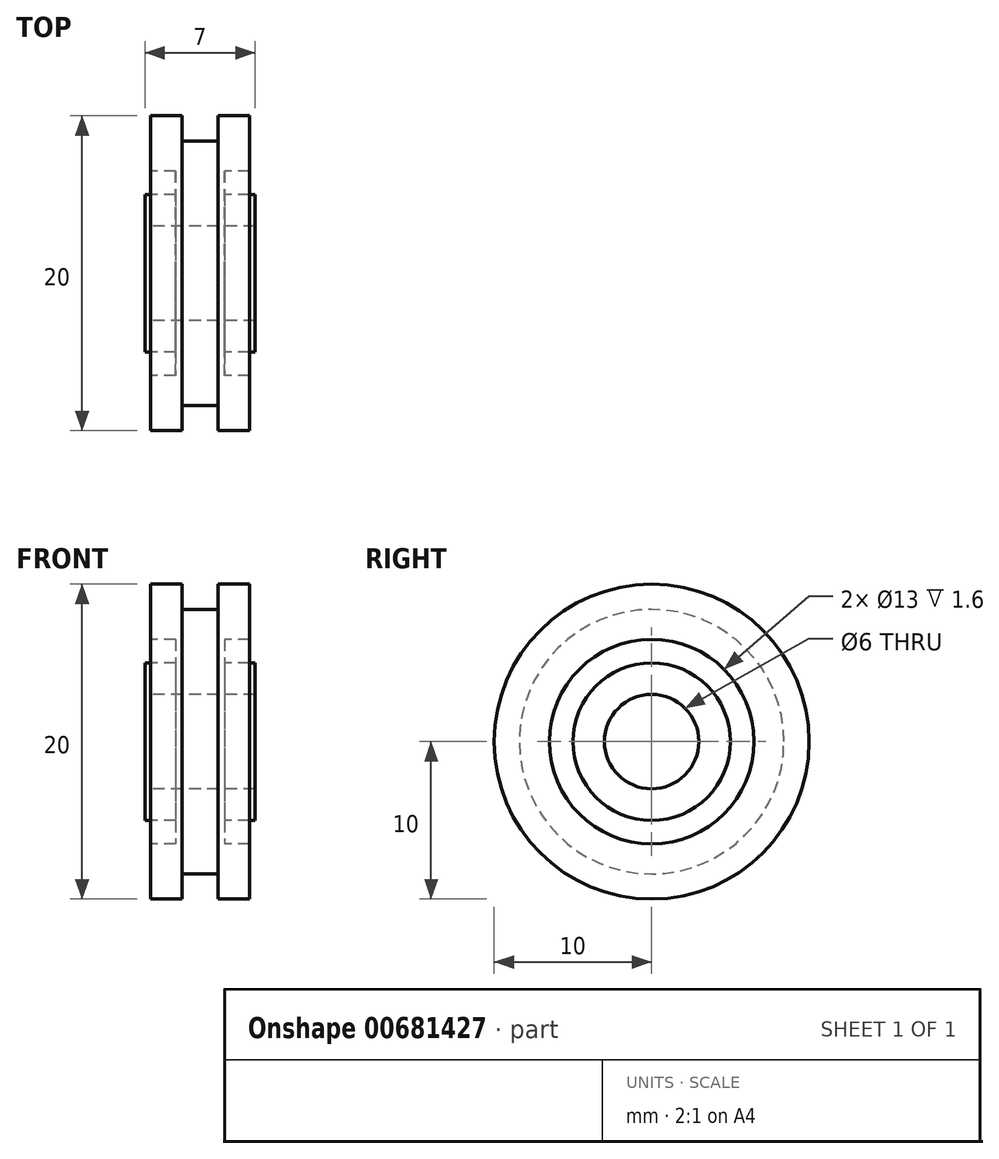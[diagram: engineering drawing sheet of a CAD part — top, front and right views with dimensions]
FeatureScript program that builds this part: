
annotation { "Feature Type Name" : "Feature", "Feature Type Description" : "" }
export const myFeature = defineFeature(function(context is Context, id is Id, definition is map)
    precondition{}
    {
        {
            var Q0;
            Q0=qCreatedBy(makeId("Front.planeOp"),FACE);
            var sketch = newSketch(context, id + "F0", { "sketchPlane" : qUnion([Q0])});
            skLineSegment(sketch, "E0", {"start": v(-1.15, 10) * mm, "end": v(-3.15, 10) * mm});
            skLineSegment(sketch, "E1", {"start": v(-3.15, 10) * mm, "end": v(-3.15, 6.5) * mm});
            skLineSegment(sketch, "E2", {"start": v(-3.15, 6.5) * mm, "end": v(-1.55, 6.5) * mm});
            skLineSegment(sketch, "E3", {"start": v(-1.55, 6.5) * mm, "end": v(-1.55, 5) * mm});
            skLineSegment(sketch, "E4", {"start": v(-1.55, 5) * mm, "end": v(-3.5, 5) * mm});
            skLineSegment(sketch, "E5", {"start": v(-3.5, 5) * mm, "end": v(-3.5, 3) * mm});
            skLineSegment(sketch, "E6", {"start": v(-3.5, 3) * mm, "end": v(0, 3) * mm});
            skLineSegment(sketch, "E7.MirrorCS", {"start": v(1.15, 10) * mm, "end": v(3.15, 10) * mm});
            skLineSegment(sketch, "E8.MirrorCS", {"start": v(3.15, 10) * mm, "end": v(3.15, 6.5) * mm});
            skLineSegment(sketch, "E9.MirrorCS", {"start": v(3.15, 6.5) * mm, "end": v(1.55, 6.5) * mm});
            skLineSegment(sketch, "E10.MirrorCS", {"start": v(1.55, 6.5) * mm, "end": v(1.55, 5) * mm});
            skLineSegment(sketch, "E11.MirrorCS", {"start": v(1.55, 5) * mm, "end": v(3.5, 5) * mm});
            skLineSegment(sketch, "E12.MirrorCS", {"start": v(3.5, 5) * mm, "end": v(3.5, 3) * mm});
            skLineSegment(sketch, "E13.MirrorCS", {"start": v(3.5, 3) * mm, "end": v(0, 3) * mm});
            skLineSegment(sketch, "E14", {"start": v(-1.15, 10) * mm, "end": v(-1.15, 8.4) * mm});
            skLineSegment(sketch, "E15", {"start": v(-1.15, 8.4) * mm, "end": v(0, 8.4) * mm});
            skLineSegment(sketch, "E16.MirrorCS", {"start": v(1.15, 8.4) * mm, "end": v(0, 8.4) * mm});
            skLineSegment(sketch, "E17.MirrorCS", {"start": v(1.15, 10) * mm, "end": v(1.15, 8.4) * mm});
            skPoint(sketch, "E18.orphan", {"position": v(0, 10) * mm});
            skLineSegment(sketch, "E19", {"start": v(-6.36, 0) * mm, "end": v(7.66, 0) * mm, "construction": true});
            skSolve(sketch);
        }
        {
            var Q0;
            Q0 = qSketchRegion(id + "F0", true);
            var Q1;
            Q1=sQuery(id+"F0.wireOp",EDGE,"E19");
            revolve(context, id + "F1", {"entities" : qUnion([Q0]), "axis" : qUnion([Q1]), "revolveType" : RevolveType.FULL});
        }
    });
